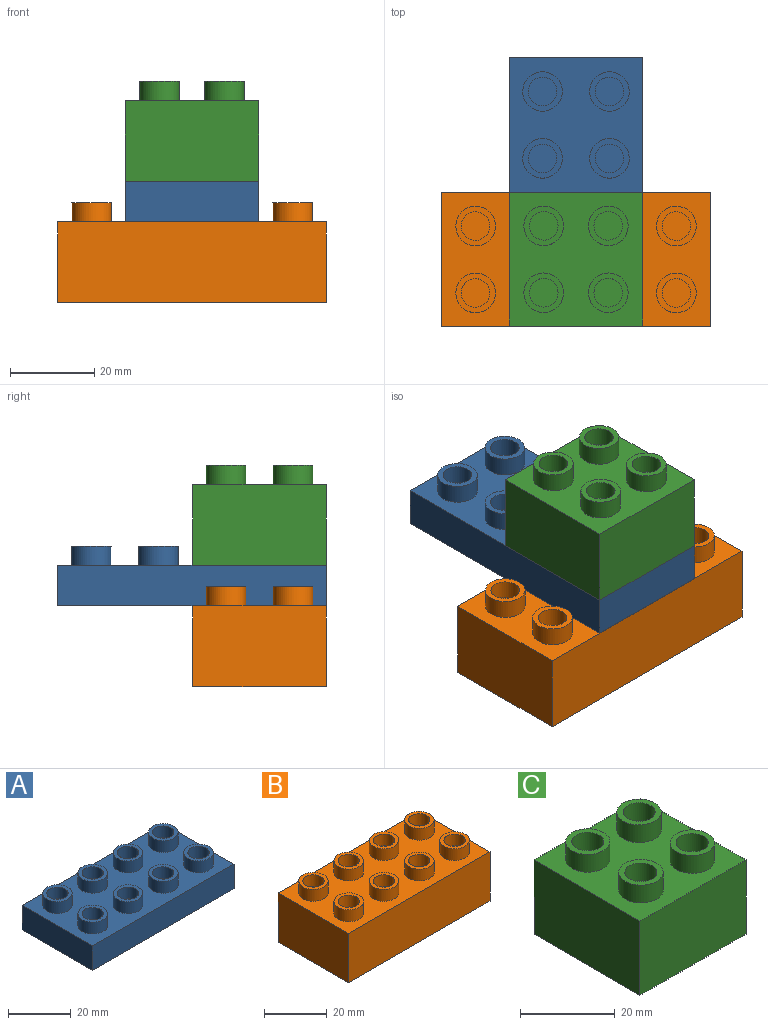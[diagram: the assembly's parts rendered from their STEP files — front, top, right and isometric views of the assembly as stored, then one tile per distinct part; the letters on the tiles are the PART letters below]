
ASSEMBLY  parts=3 mates=2
PART A: 38 faces, bbox 63.8x31.7x14.2 mm
  f0: plane 31.7x9.6mm, normal (-1,0,0), area 304.3mm2, adj f1,f3,f4,f5
  f1: plane 63.8x9.6mm, normal (0,-1,0), area 612.5mm2, adj f0,f2,f4,f5
  f2: plane 31.7x9.6mm, normal (1,0,0), area 304.3mm2, adj f1,f3,f4,f5
  f3: plane 63.8x9.6mm, normal (0,1,0), area 612.5mm2, adj f0,f2,f4,f5
  f4: plane 63.8x31.7mm, normal (0,0,1), area 1467.3mm2, adj f0,f1,f2,f3,f7,f11,f15,f19
  f5: plane 63.8x31.7mm, normal (0,0,-1), area 2022.5mm2, adj f0,f1,f2,f3
  f6: cylinder r=3.4mm len=6.8mm, axis (0,0,-1), area 98.3mm2, adj f8,f9
  f7: cylinder r=4.7mm len=9.4mm, axis (0,0,-1), area 135.8mm2, adj f4,f8
  f8: plane 9.4x9.4mm, normal (0,0,1), area 33.1mm2, adj f6,f7
  f9: plane 6.8x6.8mm, normal (0,0,1), area 36.3mm2, adj f6
  f10: cylinder r=3.4mm len=6.8mm, axis (0,0,-1), area 98.3mm2, adj f12,f13
  f11: cylinder r=4.7mm len=9.4mm, axis (0,0,-1), area 135.8mm2, adj f4,f12
  f12: plane 9.4x9.4mm, normal (0,0,1), area 33.1mm2, adj f10,f11
  f13: plane 6.8x6.8mm, normal (0,0,1), area 36.3mm2, adj f10
  f14: cylinder r=3.4mm len=6.8mm, axis (0,0,-1), area 98.3mm2, adj f16,f17
  f15: cylinder r=4.7mm len=9.4mm, axis (0,0,-1), area 135.8mm2, adj f4,f16
  f16: plane 9.4x9.4mm, normal (0,0,1), area 33.1mm2, adj f14,f15
  f17: plane 6.8x6.8mm, normal (0,0,1), area 36.3mm2, adj f14
  f18: cylinder r=3.4mm len=6.8mm, axis (0,0,-1), area 98.3mm2, adj f20,f21
  f19: cylinder r=4.7mm len=9.4mm, axis (0,0,-1), area 135.8mm2, adj f4,f20
  f20: plane 9.4x9.4mm, normal (0,0,1), area 33.1mm2, adj f18,f19
  f21: plane 6.8x6.8mm, normal (0,0,1), area 36.3mm2, adj f18
  f22: cylinder r=4.7mm len=9.4mm, axis (0,0,-1), area 135.8mm2, adj f4,f24
  f23: cylinder r=3.4mm len=6.8mm, axis (0,0,-1), area 98.3mm2, adj f24,f25
  f24: plane 9.4x9.4mm, normal (0,0,1), area 33.1mm2, adj f22,f23
  f25: plane 6.8x6.8mm, normal (0,0,1), area 36.3mm2, adj f23
  f26: cylinder r=4.7mm len=9.4mm, axis (0,0,-1), area 135.8mm2, adj f4,f28
  f27: cylinder r=3.4mm len=6.8mm, axis (0,0,-1), area 98.3mm2, adj f28,f29
  f28: plane 9.4x9.4mm, normal (0,0,1), area 33.1mm2, adj f26,f27
  f29: plane 6.8x6.8mm, normal (0,0,1), area 36.3mm2, adj f27
  f30: cylinder r=4.7mm len=9.4mm, axis (0,0,-1), area 135.8mm2, adj f4,f32
  f31: cylinder r=3.4mm len=6.8mm, axis (0,0,-1), area 98.3mm2, adj f32,f33
  f32: plane 9.4x9.4mm, normal (0,0,1), area 33.1mm2, adj f30,f31
  f33: plane 6.8x6.8mm, normal (0,0,1), area 36.3mm2, adj f31
  f34: cylinder r=4.7mm len=9.4mm, axis (0,0,-1), area 135.8mm2, adj f4,f36
  f35: cylinder r=3.4mm len=6.8mm, axis (0,0,-1), area 98.3mm2, adj f36,f37
  f36: plane 9.4x9.4mm, normal (0,0,1), area 33.1mm2, adj f34,f35
  f37: plane 6.8x6.8mm, normal (0,0,1), area 36.3mm2, adj f35
PART B: 38 faces, bbox 63.8x31.7x23.8 mm
  f0: plane 31.7x19.2mm, normal (-1,0,0), area 608.6mm2, adj f1,f3,f4,f5
  f1: plane 63.8x19.2mm, normal (0,-1,0), area 1225mm2, adj f0,f2,f4,f5
  f2: plane 31.7x19.2mm, normal (1,0,0), area 608.6mm2, adj f1,f3,f4,f5
  f3: plane 63.8x19.2mm, normal (0,1,0), area 1225mm2, adj f0,f2,f4,f5
  f4: plane 63.8x31.7mm, normal (0,0,1), area 1467.3mm2, adj f0,f1,f2,f3,f7,f11,f15,f19
  f5: plane 63.8x31.7mm, normal (0,0,-1), area 2022.5mm2, adj f0,f1,f2,f3
  f6: cylinder r=3.4mm len=6.8mm, axis (0,0,-1), area 98.3mm2, adj f8,f9
  f7: cylinder r=4.7mm len=9.4mm, axis (0,0,-1), area 135.8mm2, adj f4,f8
  f8: plane 9.4x9.4mm, normal (0,0,1), area 33.1mm2, adj f6,f7
  f9: plane 6.8x6.8mm, normal (0,0,1), area 36.3mm2, adj f6
  f10: cylinder r=3.4mm len=6.8mm, axis (0,0,-1), area 98.3mm2, adj f12,f13
  f11: cylinder r=4.7mm len=9.4mm, axis (0,0,-1), area 135.8mm2, adj f4,f12
  f12: plane 9.4x9.4mm, normal (0,0,1), area 33.1mm2, adj f10,f11
  f13: plane 6.8x6.8mm, normal (0,0,1), area 36.3mm2, adj f10
  f14: cylinder r=3.4mm len=6.8mm, axis (0,0,-1), area 98.3mm2, adj f16,f17
  f15: cylinder r=4.7mm len=9.4mm, axis (0,0,-1), area 135.8mm2, adj f4,f16
  f16: plane 9.4x9.4mm, normal (0,0,1), area 33.1mm2, adj f14,f15
  f17: plane 6.8x6.8mm, normal (0,0,1), area 36.3mm2, adj f14
  f18: cylinder r=3.4mm len=6.8mm, axis (0,0,-1), area 98.3mm2, adj f20,f21
  f19: cylinder r=4.7mm len=9.4mm, axis (0,0,-1), area 135.8mm2, adj f4,f20
  f20: plane 9.4x9.4mm, normal (0,0,1), area 33.1mm2, adj f18,f19
  f21: plane 6.8x6.8mm, normal (0,0,1), area 36.3mm2, adj f18
  f22: cylinder r=4.7mm len=9.4mm, axis (0,0,-1), area 135.8mm2, adj f4,f24
  f23: cylinder r=3.4mm len=6.8mm, axis (0,0,-1), area 98.3mm2, adj f24,f25
  f24: plane 9.4x9.4mm, normal (0,0,1), area 33.1mm2, adj f22,f23
  f25: plane 6.8x6.8mm, normal (0,0,1), area 36.3mm2, adj f23
  f26: cylinder r=4.7mm len=9.4mm, axis (0,0,-1), area 135.8mm2, adj f4,f28
  f27: cylinder r=3.4mm len=6.8mm, axis (0,0,-1), area 98.3mm2, adj f28,f29
  f28: plane 9.4x9.4mm, normal (0,0,1), area 33.1mm2, adj f26,f27
  f29: plane 6.8x6.8mm, normal (0,0,1), area 36.3mm2, adj f27
  f30: cylinder r=4.7mm len=9.4mm, axis (0,0,-1), area 135.8mm2, adj f4,f32
  f31: cylinder r=3.4mm len=6.8mm, axis (0,0,-1), area 98.3mm2, adj f32,f33
  f32: plane 9.4x9.4mm, normal (0,0,1), area 33.1mm2, adj f30,f31
  f33: plane 6.8x6.8mm, normal (0,0,1), area 36.3mm2, adj f31
  f34: cylinder r=4.7mm len=9.4mm, axis (0,0,-1), area 135.8mm2, adj f4,f36
  f35: cylinder r=3.4mm len=6.8mm, axis (0,0,-1), area 98.3mm2, adj f36,f37
  f36: plane 9.4x9.4mm, normal (0,0,1), area 33.1mm2, adj f34,f35
  f37: plane 6.8x6.8mm, normal (0,0,1), area 36.3mm2, adj f35
PART C: 22 faces, bbox 31.7x31.7x23.8 mm
  f0: plane 31.7x19.2mm, normal (-1,0,0), area 608.6mm2, adj f1,f3,f4,f5
  f1: plane 31.7x19.2mm, normal (0,-1,0), area 608.6mm2, adj f0,f2,f4,f5
  f2: plane 31.7x19.2mm, normal (1,0,0), area 608.6mm2, adj f1,f3,f4,f5
  f3: plane 31.7x19.2mm, normal (0,1,0), area 608.6mm2, adj f0,f2,f4,f5
  f4: plane 31.7x31.7mm, normal (0,0,1), area 727.3mm2, adj f0,f1,f2,f3,f7,f10,f14,f19
  f5: plane 31.7x31.7mm, normal (0,0,-1), area 1004.9mm2, adj f0,f1,f2,f3
  f6: cylinder r=3.4mm len=6.8mm, axis (0,0,-1), area 98.3mm2, adj f8,f9
  f7: cylinder r=4.7mm len=9.4mm, axis (0,0,-1), area 135.8mm2, adj f4,f8
  f8: plane 9.4x9.4mm, normal (0,0,1), area 33.1mm2, adj f6,f7
  f9: plane 6.8x6.8mm, normal (0,0,1), area 36.3mm2, adj f6
  f10: cylinder r=4.7mm len=9.4mm, axis (0,0,-1), area 135.8mm2, adj f4,f12
  f11: cylinder r=3.4mm len=6.8mm, axis (0,0,-1), area 98.3mm2, adj f12,f13
  f12: plane 9.4x9.4mm, normal (0,0,1), area 33.1mm2, adj f10,f11
  f13: plane 6.8x6.8mm, normal (0,0,1), area 36.3mm2, adj f11
  f14: cylinder r=4.7mm len=9.4mm, axis (0,0,-1), area 135.8mm2, adj f4,f16
  f15: cylinder r=3.4mm len=6.8mm, axis (0,0,-1), area 98.3mm2, adj f16,f17
  f16: plane 9.4x9.4mm, normal (0,0,1), area 33.1mm2, adj f14,f15
  f17: plane 6.8x6.8mm, normal (0,0,1), area 36.3mm2, adj f15
  f18: cylinder r=3.4mm len=6.8mm, axis (0,0,-1), area 98.3mm2, adj f20,f21
  f19: cylinder r=4.7mm len=9.4mm, axis (0,0,-1), area 135.8mm2, adj f4,f20
  f20: plane 9.4x9.4mm, normal (0,0,1), area 33.1mm2, adj f18,f19
  f21: plane 6.8x6.8mm, normal (0,0,1), area 36.3mm2, adj f18
PLACE A rot(axis=(0,0,1),90deg) t=(0,16.05,19.2)mm
PLACE B at identity
PLACE C t=(0,0,28.8)mm
MATE fastened C.f5 <-> A.f4  axis (0,0,-1) through (0,-15.85,28.8)mm
MATE fastened B.f4 <-> A.f5  axis (0,0,1) through (0,-15.85,19.2)mm
